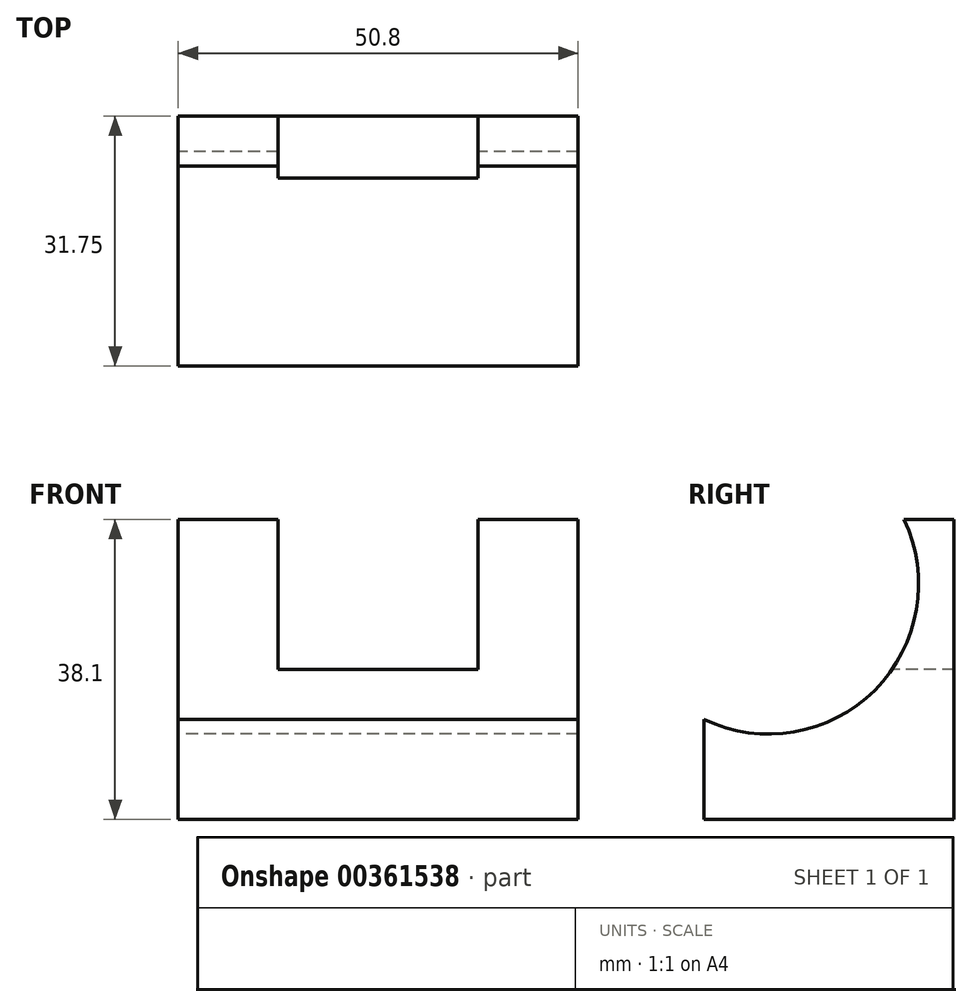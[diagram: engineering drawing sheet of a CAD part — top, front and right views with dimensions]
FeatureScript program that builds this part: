
annotation { "Feature Type Name" : "Feature", "Feature Type Description" : "" }
export const myFeature = defineFeature(function(context is Context, id is Id, definition is map)
    precondition{}
    {
        {
            var Q0;
            Q0=qCreatedBy(makeId("Right.planeOp"),FACE);
            var sketch = newSketch(context, id + "F0", { "sketchPlane" : qUnion([Q0])});
            skLineSegment(sketch, "E0", {"start": v(0, 38.1) * mm, "end": v(0, 0) * mm});
            skLineSegment(sketch, "E1", {"start": v(0, 0) * mm, "end": v(-31.75, 0) * mm});
            skLineSegment(sketch, "E2", {"start": v(-31.75, 0) * mm, "end": v(-31.75, 12.7) * mm});
            skLineSegment(sketch, "E3", {"start": v(0, 38.1) * mm, "end": v(-6.35, 38.1) * mm});
            skArc(sketch, "E4", {"start": v(-31.75, 12.7) * mm, "mid": v(-10.07, 16.42) * mm, "end": v(-6.35, 38.1) * mm});
            skSolve(sketch);
        }
        {
            var Q0;
            Q0 = qSketchRegion(id + "F0", true);
            extrude(context, id + "F1", {"entities" : qUnion([Q0]), "depth" : 50.8 * mm});
        }
        {
            var Q0;
            Q0=makeQuery(id+"F1.opExtrude","SWEPT_FACE",FACE,{"disambiguationData":[OSD([sQuery(id+"F0.wireOp",EDGE,"E3")])]});
            var sketch = newSketch(context, id + "F2", { "sketchPlane" : qUnion([Q0])});
            skLineSegment(sketch, "E5.bottom", {"start": v(12.7, 0) * mm, "end": v(38.1, 0) * mm});
            skLineSegment(sketch, "E5.top", {"start": v(12.7, -15.88) * mm, "end": v(38.1, -15.88) * mm});
            skLineSegment(sketch, "E5.left", {"start": v(12.7, 0) * mm, "end": v(12.7, -15.88) * mm});
            skLineSegment(sketch, "E5.right", {"start": v(38.1, 0) * mm, "end": v(38.1, -15.88) * mm});
            skSolve(sketch);
        }
        {
            var Q0;
            Q0 = qSketchRegion(id + "F2", true);
            extrude(context, id + "F3", {"entities" : qUnion([Q0]), "operationType" : NewBodyOperationType.REMOVE, "oppositeDirection" : true, "depth" : 19.05 * mm});
        }
    });
